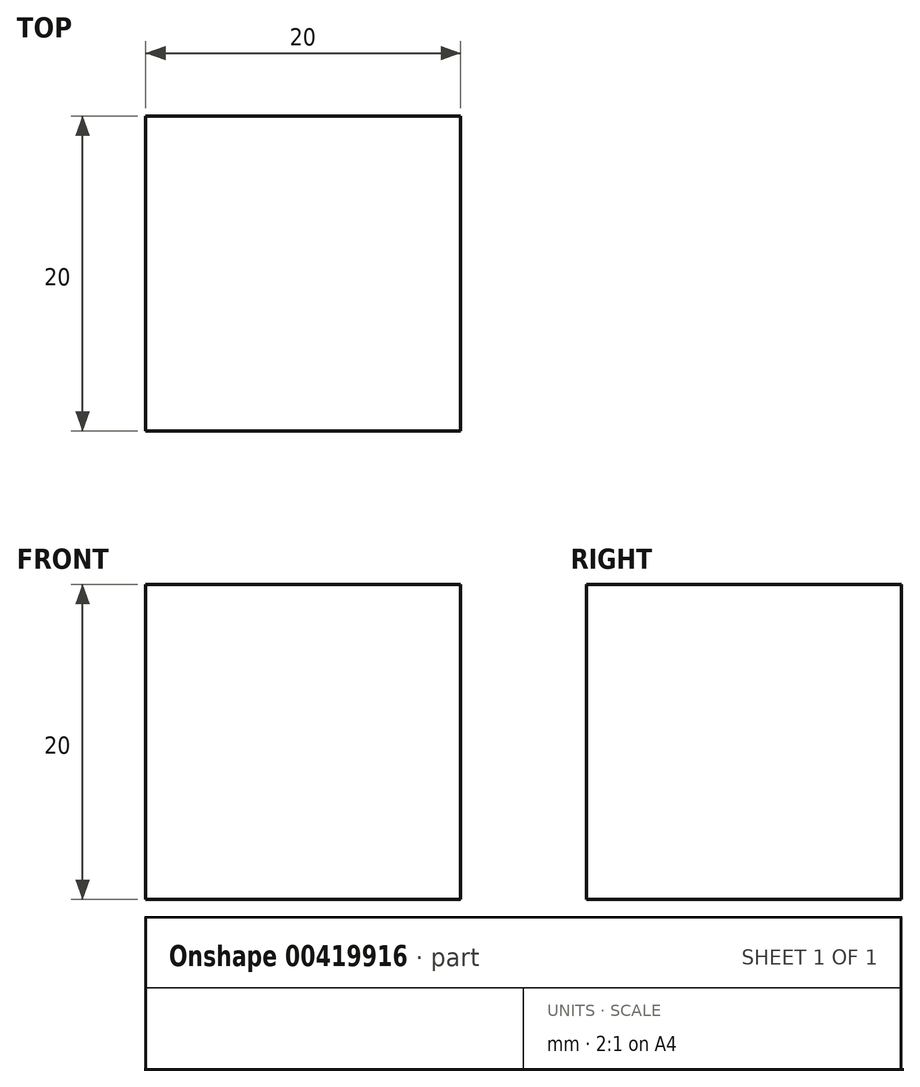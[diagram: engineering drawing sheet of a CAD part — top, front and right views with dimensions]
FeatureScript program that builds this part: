
annotation { "Feature Type Name" : "Feature", "Feature Type Description" : "" }
export const myFeature = defineFeature(function(context is Context, id is Id, definition is map)
    precondition{}
    {
        {
            var Q0;
            Q0=qCreatedBy(makeId("Top.planeOp"),FACE);
            var sketch = newSketch(context, id + "F0", { "sketchPlane" : qUnion([Q0])});
            skLineSegment(sketch, "E0.bottom", {"start": v(0, 0) * mm, "end": v(20, 0) * mm});
            skLineSegment(sketch, "E0.top", {"start": v(0, 20) * mm, "end": v(20, 20) * mm});
            skLineSegment(sketch, "E0.left", {"start": v(0, 0) * mm, "end": v(0, 20) * mm});
            skLineSegment(sketch, "E0.right", {"start": v(20, 0) * mm, "end": v(20, 20) * mm});
            skSolve(sketch);
        }
        {
            var Q0;
            Q0 = qSketchRegion(id + "F0", true);
            extrude(context, id + "F1", {"entities" : qUnion([Q0]), "depth" : 20 * mm, "offsetDistance" : 25 * mm});
        }
    });
